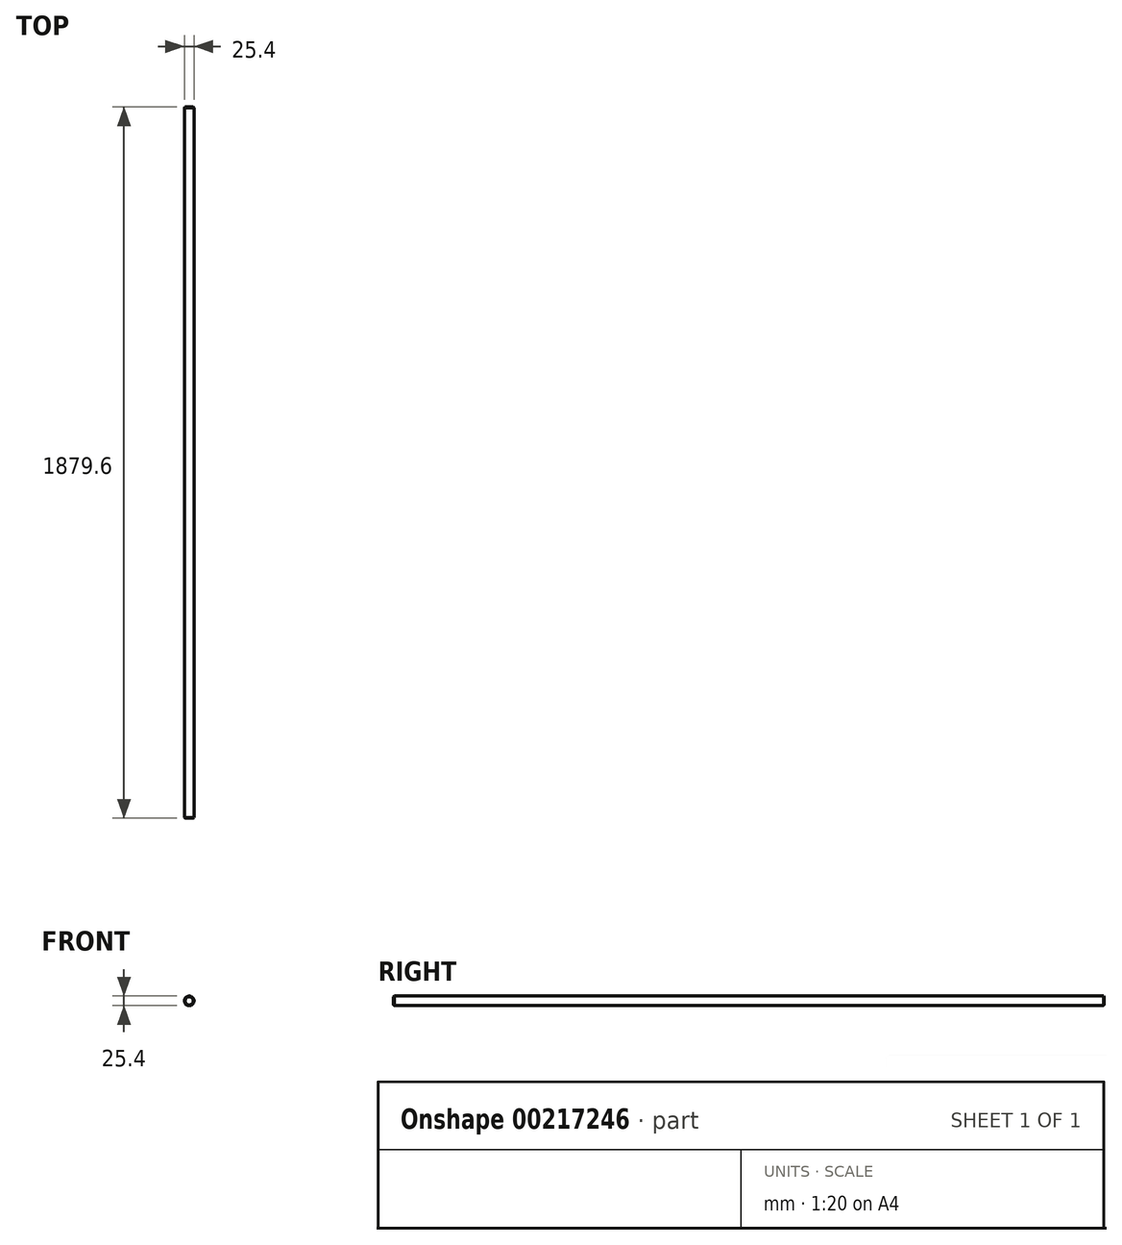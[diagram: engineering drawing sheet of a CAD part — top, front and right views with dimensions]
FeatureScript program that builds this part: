
annotation { "Feature Type Name" : "Feature", "Feature Type Description" : "" }
export const myFeature = defineFeature(function(context is Context, id is Id, definition is map)
    precondition{}
    {
        {
            var Q0;
            Q0=qCreatedBy(makeId("Front.planeOp"),FACE);
            var sketch = newSketch(context, id + "F0", { "sketchPlane" : qUnion([Q0])});
            skCircle(sketch, "E0", {"center": v(0, 0) * mm, "radius": 12.7 * mm});
            skSolve(sketch);
        }
        {
            var Q0;
            Q0 = qSketchRegion(id + "F0", true);
            extrude(context, id + "F1", {"entities" : qUnion([Q0]), "depth" : 1879.6 * mm, "offsetDistance" : 25.4 * mm});
        }
        {
            var Q0;
            Q0=makeQuery(id+"F1.opExtrude","CAP_EDGE",EDGE,{"disambiguationData":[OSD([sQuery(id+"F0.wireOp",EDGE,"E0")])],"isStart":false});
            chamfer(context, id + "F2", {"entities" : qUnion([Q0]), "chamferType" : ChamferType.OFFSET_ANGLE, "width" : 2.03 * mm, "oppositeDirection" : false, "angle" : 45 * degree, "tangentPropagation" : true});
        }
        {
            var Q0;
            Q0=makeQuery(id+"F1.opExtrude","CAP_EDGE",EDGE,{"disambiguationData":[OSD([sQuery(id+"F0.wireOp",EDGE,"E0")])],"isStart":true});
            chamfer(context, id + "F3", {"entities" : qUnion([Q0]), "chamferType" : ChamferType.OFFSET_ANGLE, "width" : 2.03 * mm, "oppositeDirection" : false, "angle" : 45 * degree, "tangentPropagation" : true});
        }
    });
